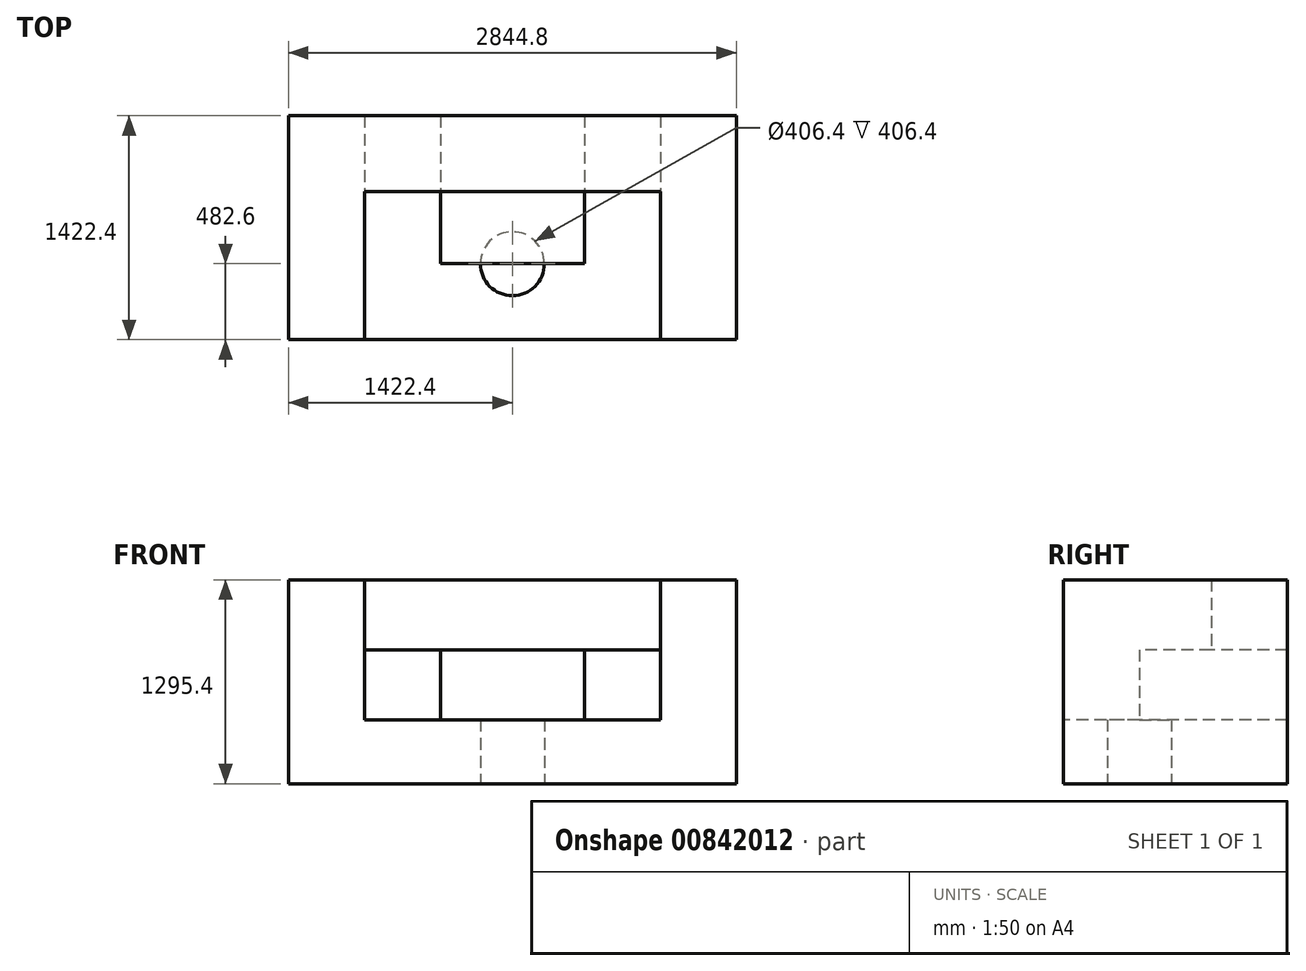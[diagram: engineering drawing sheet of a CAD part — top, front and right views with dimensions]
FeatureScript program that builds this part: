
annotation { "Feature Type Name" : "Feature", "Feature Type Description" : "" }
export const myFeature = defineFeature(function(context is Context, id is Id, definition is map)
    precondition{}
    {
        {
            var Q0;
            Q0=qCreatedBy(makeId("Front.planeOp"),FACE);
            var sketch = newSketch(context, id + "F0", { "sketchPlane" : qUnion([Q0])});
            skLineSegment(sketch, "E0.bottom", {"start": v(0, 0) * mm, "end": v(2844.8, 0) * mm});
            skLineSegment(sketch, "E0.top", {"start": v(0, 1295.4) * mm, "end": v(2844.8, 1295.4) * mm});
            skLineSegment(sketch, "E0.left", {"start": v(0, 0) * mm, "end": v(0, 1295.4) * mm});
            skLineSegment(sketch, "E0.right", {"start": v(2844.8, 0) * mm, "end": v(2844.8, 1295.4) * mm});
            skSolve(sketch);
        }
        {
            var Q0;
            Q0 = qSketchRegion(id + "F0", true);
            extrude(context, id + "F1", {"entities" : qUnion([Q0]), "depth" : 1447.8 * mm, "offsetDistance" : 25.4 * mm});
        }
        {
            var Q0;
            Q0=makeQuery(id+"F1.opExtrude","CAP_FACE",FACE,{"disambiguationData":[OSD([sQuery(id+"F0.wireOp",EDGE,"E0.bottom"),sQuery(id+"F0.wireOp",EDGE,"E0.top"),sQuery(id+"F0.wireOp",EDGE,"E0.left"),sQuery(id+"F0.wireOp",EDGE,"E0.right")])],"isStart":false});
            var sketch = newSketch(context, id + "F2", { "sketchPlane" : qUnion([Q0])});
            skLineSegment(sketch, "E1", {"start": v(0, 1295.4) * mm, "end": v(482.6, 1295.4) * mm});
            skLineSegment(sketch, "E2", {"start": v(482.6, 1295.4) * mm, "end": v(482.6, 406.4) * mm});
            skLineSegment(sketch, "E3", {"start": v(482.6, 406.4) * mm, "end": v(2362.2, 406.4) * mm});
            skLineSegment(sketch, "E4", {"start": v(2362.2, 406.4) * mm, "end": v(2362.2, 1295.4) * mm});
            skLineSegment(sketch, "E5", {"start": v(2362.2, 1295.4) * mm, "end": v(2844.8, 1295.4) * mm});
            skLineSegment(sketch, "E6", {"start": v(482.6, 850.9) * mm, "end": v(2362.2, 850.9) * mm});
            skLineSegment(sketch, "E7", {"start": v(965.2, 850.9) * mm, "end": v(965.2, 406.4) * mm});
            skLineSegment(sketch, "E8", {"start": v(1879.6, 850.9) * mm, "end": v(1879.6, 406.4) * mm});
            skLineSegment(sketch, "E9", {"start": v(965.2, 850.9) * mm, "end": v(482.6, 850.9) * mm});
            skLineSegment(sketch, "E10", {"start": v(1879.6, 850.9) * mm, "end": v(2362.2, 850.9) * mm});
            skLineSegment(sketch, "E11", {"start": v(869.32, 406.4) * mm, "end": v(869.32, 0) * mm});
            skSolve(sketch);
        }
        {
            var Q0;
            {var subQ5=sQuery(id+"F2.wireOp",EDGE,"E1");Q0=makeQuery(id+"F2.imprint","IMPRINT",FACE,{"disambiguationData":[TD([[makeQuery(id+"F2.imprint","IMPRINT",EDGE,{"derivedFrom":subQ5}),-1.0]])]});}
            var sketch = newSketch(context, id + "F3", { "sketchPlane" : qUnion([Q0])});
            skLineSegment(sketch, "E12", {"start": v(483.39, 855.54) * mm, "end": v(483.39, 408.37) * mm});
            skLineSegment(sketch, "E13", {"start": v(483.39, 408.37) * mm, "end": v(967.38, 408.37) * mm});
            skLineSegment(sketch, "E14", {"start": v(967.38, 408.37) * mm, "end": v(967.38, 850.28) * mm});
            skLineSegment(sketch, "E15", {"start": v(967.38, 850.28) * mm, "end": v(483.39, 855.54) * mm});
            skLineSegment(sketch, "E16", {"start": v(1882.76, 408.37) * mm, "end": v(1882.76, 855.54) * mm});
            skLineSegment(sketch, "E17", {"start": v(1882.76, 855.54) * mm, "end": v(2361.5, 855.54) * mm});
            skLineSegment(sketch, "E18", {"start": v(2361.5, 855.54) * mm, "end": v(2361.5, 413.63) * mm});
            skLineSegment(sketch, "E19", {"start": v(2361.5, 413.63) * mm, "end": v(1882.76, 408.37) * mm});
            skSolve(sketch);
        }
        {
            var Q0;
            Q0=makeQuery(id+"F2.imprint","IMPRINT",FACE,{"disambiguationData":[TD([[makeQuery(id+"F2.imprint","IMPRINT",EDGE,{"derivedFrom":sQuery(id+"F2.wireOp",EDGE,"E6")}),1.0]])]});
            var Q1;
            {var subQ0=sQuery(id+"F2.wireOp",EDGE,"E7");Q1=makeQuery(id+"F2.imprint","IMPRINT",FACE,{"disambiguationData":[TD([[makeQuery(id+"F2.imprint","IMPRINT",EDGE,{"derivedFrom":subQ0}),-1.0]])]});}
            var Q2;
            {var subQ3=sQuery(id+"F2.wireOp",EDGE,"E8");Q2=makeQuery(id+"F2.imprint","IMPRINT",FACE,{"disambiguationData":[TD([[makeQuery(id+"F2.imprint","IMPRINT",EDGE,{"derivedFrom":subQ3}),1.0]])]});}
            extrude(context, id + "F4", {"entities" : qUnion([Q0, Q1, Q2]), "operationType" : NewBodyOperationType.REMOVE, "oppositeDirection" : true, "depth" : 965.2 * mm, "offsetDistance" : 25.4 * mm});
        }
        {
            var Q0;
            Q0=makeQuery(id+"F4.boolean.opBoolean","COPY",FACE,{"derivedFrom":makeQuery(id+"F4.opExtrude","CAP_FACE",FACE,{"disambiguationData":[OSD([sQuery(id+"F0.wireOp",EDGE,"E0.top"),sQuery(id+"F2.wireOp",EDGE,"E2"),sQuery(id+"F2.wireOp",EDGE,"E3"),sQuery(id+"F2.wireOp",EDGE,"E4"),sQuery(id+"F2.wireOp",EDGE,"E6"),sQuery(id+"F2.wireOp",EDGE,"E7"),sQuery(id+"F2.wireOp",EDGE,"E8")])],"isStart":false})});
            var sketch = newSketch(context, id + "F5", { "sketchPlane" : qUnion([Q0])});
            skLineSegment(sketch, "E20", {"start": v(965.2, 850.9) * mm, "end": v(482.6, 850.9) * mm});
            skLineSegment(sketch, "E21", {"start": v(1879.6, 850.9) * mm, "end": v(2362.2, 850.9) * mm});
            skSolve(sketch);
        }
        {
            var Q0;
            Q0 = qSketchRegion(id + "F5", true);
            var Q1;
            {var subQ0=sQuery(id+"F5.wireOp",EDGE,"E20");Q1=makeQuery(id+"F5.imprint","IMPRINT",FACE,{"disambiguationData":[TD([[makeQuery(id+"F5.imprint","IMPRINT",EDGE,{"derivedFrom":subQ0}),1.0]])]});}
            var Q2;
            {var subQ0=sQuery(id+"F5.wireOp",EDGE,"E21");Q2=makeQuery(id+"F5.imprint","IMPRINT",FACE,{"disambiguationData":[TD([[makeQuery(id+"F5.imprint","IMPRINT",EDGE,{"derivedFrom":subQ0}),-1.0]])]});}
            extrude(context, id + "F6", {"entities" : qUnion([Q0, Q1, Q2]), "operationType" : NewBodyOperationType.REMOVE, "oppositeDirection" : true, "depth" : 508 * mm, "offsetDistance" : 25.4 * mm});
        }
        {
            var Q0;
            Q0=makeQuery(id+"F1.opExtrude","CAP_FACE",FACE,{"disambiguationData":[OSD([sQuery(id+"F0.wireOp",EDGE,"E0.bottom"),sQuery(id+"F0.wireOp",EDGE,"E0.top"),sQuery(id+"F0.wireOp",EDGE,"E0.left"),sQuery(id+"F0.wireOp",EDGE,"E0.right")])],"isStart":false});
            var sketch = newSketch(context, id + "F7", { "sketchPlane" : qUnion([Q0])});
            skLineSegment(sketch, "E22", {"start": v(967.38, 408.37) * mm, "end": v(1879.6, 406.4) * mm});
            skSolve(sketch);
        }
        {
            var Q0;
            {var subQ6=sQuery(id+"F0.wireOp",EDGE,"E0.bottom");Q0=makeQuery(id+"F7.imprint","IMPRINT",FACE,{"disambiguationData":[TD([[makeQuery(id+"F7.imprint","IMPRINT",EDGE,{"derivedFrom":makeQuery(id+"F1.opExtrude","CAP_EDGE",EDGE,{"disambiguationData":[OSD([subQ6])],"isStart":false})}),1.0]])]});}
            extrude(context, id + "F8", {"entities" : qUnion([Q0]), "operationType" : NewBodyOperationType.REMOVE, "oppositeDirection" : true, "depth" : 25.4 * mm, "offsetDistance" : 25.4 * mm});
        }
        {
            var Q0;
            Q0=makeQuery(id+"F8.boolean.opBoolean","COPY",FACE,{"derivedFrom":makeQuery(id+"F8.opExtrude","CAP_FACE",FACE,{"disambiguationData":[OSD([sQuery(id+"F0.wireOp",EDGE,"E0.bottom"),sQuery(id+"F0.wireOp",EDGE,"E0.top"),sQuery(id+"F0.wireOp",EDGE,"E0.left"),sQuery(id+"F0.wireOp",EDGE,"E0.right"),sQuery(id+"F2.wireOp",EDGE,"E2"),sQuery(id+"F2.wireOp",EDGE,"E3"),sQuery(id+"F2.wireOp",EDGE,"E4"),sQuery(id+"F2.wireOp",EDGE,"E6"),sQuery(id+"F2.wireOp",EDGE,"E7"),sQuery(id+"F2.wireOp",EDGE,"E8")])],"isStart":false})});
            var sketch = newSketch(context, id + "F9", { "sketchPlane" : qUnion([Q0])});
            skLineSegment(sketch, "E23", {"start": v(965.2, 406.4) * mm, "end": v(1879.6, 406.4) * mm});
            skLineSegment(sketch, "E24", {"start": v(1879.6, 406.4) * mm, "end": v(1879.6, 850.9) * mm});
            skLineSegment(sketch, "E25", {"start": v(1879.6, 850.9) * mm, "end": v(965.2, 850.9) * mm});
            skLineSegment(sketch, "E26", {"start": v(965.2, 850.9) * mm, "end": v(965.2, 406.4) * mm});
            skSolve(sketch);
        }
        {
            var Q0;
            Q0=makeQuery(id+"F9.imprint","IMPRINT",FACE,{"disambiguationData":[TD([[makeQuery(id+"F9.imprint","IMPRINT",EDGE,{"derivedFrom":sQuery(id+"F9.wireOp",EDGE,"E23")}),1.0]])]});
            extrude(context, id + "F10", {"entities" : qUnion([Q0]), "operationType" : NewBodyOperationType.REMOVE, "oppositeDirection" : true, "depth" : 482.6 * mm, "offsetDistance" : 25.4 * mm});
        }
        {
            var Q0;
            Q0=makeQuery(id+"F1.opExtrude","SWEPT_FACE",FACE,{"disambiguationData":[OSD([sQuery(id+"F0.wireOp",EDGE,"E0.bottom")])]});
            var sketch = newSketch(context, id + "F11", { "sketchPlane" : qUnion([Q0])});
            skLineSegment(sketch, "E27", {"start": v(2844.8, 1422.4) * mm, "end": v(1422.4, 1422.4) * mm});
            skLineSegment(sketch, "E28", {"start": v(1422.4, 1422.4) * mm, "end": v(1422.4, 939.8) * mm});
            skCircle(sketch, "E29", {"center": v(1422.4, 939.8) * mm, "radius": 203.2 * mm});
            skSolve(sketch);
        }
        {
            var Q0;
            Q0=makeQuery(id+"F11.imprint","IMPRINT",FACE,{"disambiguationData":[TD([[makeQuery(id+"F11.imprint","IMPRINT",EDGE,{"derivedFrom":sQuery(id+"F11.wireOp",EDGE,"E29")}),1.0]])]});
            extrude(context, id + "F12", {"entities" : qUnion([Q0]), "operationType" : NewBodyOperationType.REMOVE, "oppositeDirection" : true, "depth" : 406.4 * mm, "offsetDistance" : 25.4 * mm});
        }
    });
